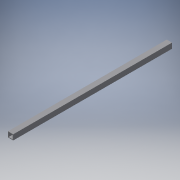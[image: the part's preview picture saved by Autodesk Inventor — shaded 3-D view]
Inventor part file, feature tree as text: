
AUTODESK INVENTOR PART (.ipt)
format: ipt  version: 2016 (Build 200138000, 138)  size: 104,448 bytes
history: native  units: in
note: dims shown in document units (in); Inventor stores cm internally (conversion verified against a paired STEP export)
features: extrude x2, sketch x2
ambient origin geometry x8: Origin, YZ Plane, XZ Plane, XY Plane, X Axis, Y Axis, Z Axis, Center Point
bodies: Solid1 (feature_tree)
feature tree (4):
  extrude  "Extrusion1"  Depth=1.0in
  extrude  "Extrusion2"  Depth=30.0in TaperAngle=0.0deg
  sketch  "Sketch1"  dims[d0=1.0in d1=1.0in]
  sketch  "Sketch2"  dims[d2=0.125in d3=30.0in d4=0.0in d5=0.5in d6=0.5in d7=0.5in d8=1.0in d9=0.0in]
